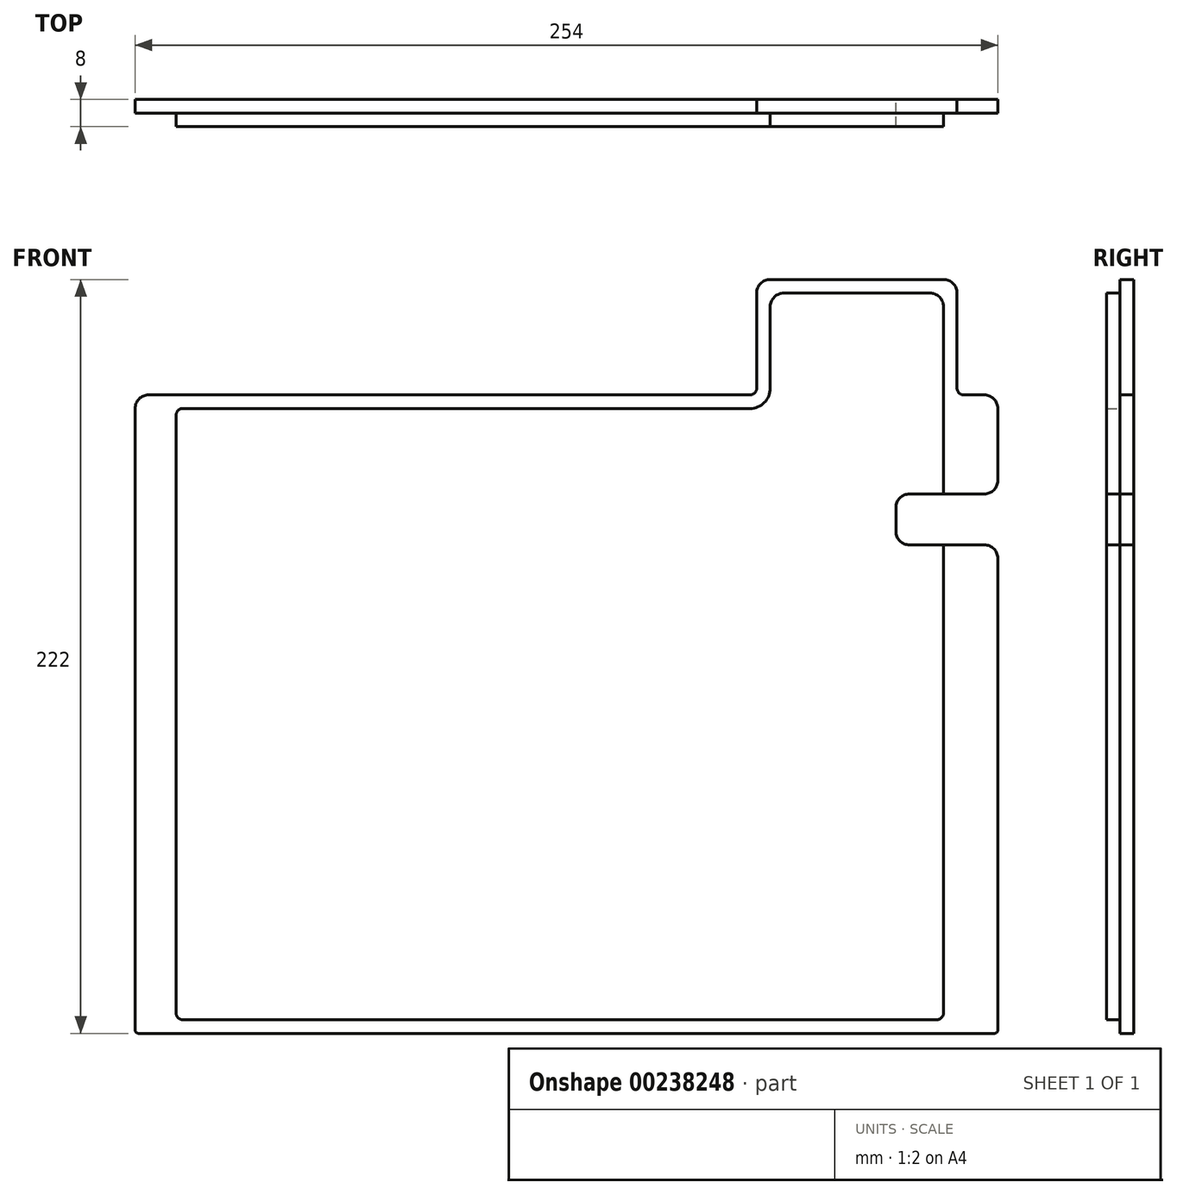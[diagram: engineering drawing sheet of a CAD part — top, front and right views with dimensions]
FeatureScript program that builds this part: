
annotation { "Feature Type Name" : "Feature", "Feature Type Description" : "" }
export const myFeature = defineFeature(function(context is Context, id is Id, definition is map)
    precondition{}
    {
        {
            var Q0;
            Q0=qCreatedBy(makeId("Front.planeOp"),FACE);
            var sketch = newSketch(context, id + "F0", { "sketchPlane" : qUnion([Q0])});
            skLineSegment(sketch, "E0.bottom", {"start": v(123, 94) * mm, "end": v(117, 94) * mm});
            skLineSegment(sketch, "E0.top", {"start": v(126, -94) * mm, "end": v(-126, -94) * mm});
            skLineSegment(sketch, "E0.left", {"start": v(127, 90) * mm, "end": v(127, 68.84) * mm});
            skLineSegment(sketch, "E0.right", {"start": v(-127, 90) * mm, "end": v(-127, -93) * mm});
            skPoint(sketch, "E0.middle", {"position": v(0, 0) * mm});
            skLineSegment(sketch, "E1.top", {"start": v(111, 128) * mm, "end": v(60, 128) * mm});
            skLineSegment(sketch, "E1.left", {"start": v(115, 96) * mm, "end": v(115, 124) * mm});
            skLineSegment(sketch, "E1.right", {"start": v(56, 96) * mm, "end": v(56, 124) * mm});
            skLineSegment(sketch, "E2.trimOffspring", {"start": v(54, 94) * mm, "end": v(-123, 94) * mm});
            skPoint(sketch, "E3.visualSharp", {"position": v(56, 128) * mm});
            skArc(sketch, "E3.filletArc", {"start": v(60, 128) * mm, "mid": v(57.17, 126.83) * mm, "end": v(56, 124) * mm});
            skPoint(sketch, "E4.visualSharp", {"position": v(115, 128) * mm});
            skArc(sketch, "E4.filletArc", {"start": v(115, 124) * mm, "mid": v(113.83, 126.83) * mm, "end": v(111, 128) * mm});
            skPoint(sketch, "E5.visualSharp", {"position": v(127, 94) * mm});
            skArc(sketch, "E5.filletArc", {"start": v(127, 90) * mm, "mid": v(125.83, 92.83) * mm, "end": v(123, 94) * mm});
            skPoint(sketch, "E6.visualSharp", {"position": v(-127, 94) * mm});
            skArc(sketch, "E6.filletArc", {"start": v(-123, 94) * mm, "mid": v(-125.83, 92.83) * mm, "end": v(-127, 90) * mm});
            skPoint(sketch, "E7.visualSharp", {"position": v(56, 94) * mm});
            skArc(sketch, "E7.filletArc", {"start": v(54, 94) * mm, "mid": v(55.41, 94.59) * mm, "end": v(56, 96) * mm});
            skPoint(sketch, "E8.visualSharp", {"position": v(115, 94) * mm});
            skArc(sketch, "E8.filletArc", {"start": v(115, 96) * mm, "mid": v(115.59, 94.59) * mm, "end": v(117, 94) * mm});
            skPoint(sketch, "E9.visualSharp", {"position": v(-127, -94) * mm});
            skArc(sketch, "E9.filletArc", {"start": v(-127, -93) * mm, "mid": v(-126.7, -93.7) * mm, "end": v(-126, -94) * mm});
            skPoint(sketch, "E10.visualSharp", {"position": v(127, -94) * mm});
            skArc(sketch, "E10.filletArc", {"start": v(126, -94) * mm, "mid": v(126.7, -93.7) * mm, "end": v(127, -93) * mm});
            skLineSegment(sketch, "E11.bottom", {"start": v(123, 64.84) * mm, "end": v(101, 64.84) * mm});
            skLineSegment(sketch, "E11.top", {"start": v(123, 49.84) * mm, "end": v(101, 49.84) * mm});
            skLineSegment(sketch, "E11.right", {"start": v(97, 60.84) * mm, "end": v(97, 53.84) * mm});
            skLineSegment(sketch, "E12.trimOffspring", {"start": v(127, 45.84) * mm, "end": v(127, -93) * mm});
            skPoint(sketch, "E13.visualSharp", {"position": v(97, 64.84) * mm});
            skArc(sketch, "E13.filletArc", {"start": v(101, 64.84) * mm, "mid": v(98.17, 63.67) * mm, "end": v(97, 60.84) * mm});
            skPoint(sketch, "E14.visualSharp", {"position": v(97, 49.84) * mm});
            skArc(sketch, "E14.filletArc", {"start": v(97, 53.84) * mm, "mid": v(98.17, 51.01) * mm, "end": v(101, 49.84) * mm});
            skPoint(sketch, "E15.visualSharp", {"position": v(127, 64.84) * mm});
            skArc(sketch, "E15.filletArc", {"start": v(123, 64.84) * mm, "mid": v(125.83, 66.01) * mm, "end": v(127, 68.84) * mm});
            skPoint(sketch, "E16.visualSharp", {"position": v(127, 49.84) * mm});
            skArc(sketch, "E16.filletArc", {"start": v(127, 45.84) * mm, "mid": v(125.83, 48.67) * mm, "end": v(123, 49.84) * mm});
            skSolve(sketch);
        }
        {
            var Q0;
            Q0=makeQuery(id+"F0.imprint","IMPRINT",FACE,{"disambiguationData":[TD([[makeQuery(id+"F0.imprint","IMPRINT",EDGE,{"derivedFrom":sQuery(id+"F0.wireOp",EDGE,"E0.bottom")}),1.0]])]});
            extrude(context, id + "F1", {"entities" : qUnion([Q0]), "depth" : 4 * mm});
        }
        {
            var Q0;
            Q0=makeQuery(id+"F1.opExtrude","CAP_FACE",FACE,{"disambiguationData":[OSD([sQuery(id+"F0.wireOp",EDGE,"E0.bottom"),sQuery(id+"F0.wireOp",EDGE,"E0.top"),sQuery(id+"F0.wireOp",EDGE,"E0.left"),sQuery(id+"F0.wireOp",EDGE,"E0.right"),sQuery(id+"F0.wireOp",EDGE,"E1.top"),sQuery(id+"F0.wireOp",EDGE,"E1.left"),sQuery(id+"F0.wireOp",EDGE,"E1.right"),sQuery(id+"F0.wireOp",EDGE,"E2.trimOffspring"),sQuery(id+"F0.wireOp",EDGE,"E3.filletArc"),sQuery(id+"F0.wireOp",EDGE,"E4.filletArc"),sQuery(id+"F0.wireOp",EDGE,"E5.filletArc"),sQuery(id+"F0.wireOp",EDGE,"E6.filletArc"),sQuery(id+"F0.wireOp",EDGE,"E7.filletArc"),sQuery(id+"F0.wireOp",EDGE,"E8.filletArc"),sQuery(id+"F0.wireOp",EDGE,"E9.filletArc"),sQuery(id+"F0.wireOp",EDGE,"E10.filletArc")])],"isStart":false});
            var sketch = newSketch(context, id + "F2", { "sketchPlane" : qUnion([Q0])});
            skLineSegment(sketch, "E17.0", {"start": v(123, 94) * mm, "end": v(117, 94) * mm, "construction": true});
            skLineSegment(sketch, "E17.1", {"start": v(126, -94) * mm, "end": v(-126, -94) * mm, "construction": true});
            skLineSegment(sketch, "E17.2", {"start": v(127, 90) * mm, "end": v(127, 68.84) * mm, "construction": true});
            skLineSegment(sketch, "E17.3", {"start": v(-127, 90) * mm, "end": v(-127, -93) * mm, "construction": true});
            skPoint(sketch, "E17.4", {"position": v(0, 0) * mm});
            skLineSegment(sketch, "E17.5", {"start": v(111, 128) * mm, "end": v(60, 128) * mm, "construction": true});
            skLineSegment(sketch, "E17.6", {"start": v(115, 96) * mm, "end": v(115, 124) * mm, "construction": true});
            skLineSegment(sketch, "E17.7", {"start": v(56, 96) * mm, "end": v(56, 124) * mm, "construction": true});
            skLineSegment(sketch, "E17.8", {"start": v(54, 94) * mm, "end": v(-123, 94) * mm, "construction": true});
            skPoint(sketch, "E17.9", {"position": v(56, 128) * mm});
            skArc(sketch, "E17.10", {"start": v(60, 128) * mm, "mid": v(57.17, 126.83) * mm, "end": v(56, 124) * mm, "construction": true});
            skPoint(sketch, "E17.11", {"position": v(115, 128) * mm});
            skArc(sketch, "E17.12", {"start": v(115, 124) * mm, "mid": v(113.83, 126.83) * mm, "end": v(111, 128) * mm, "construction": true});
            skPoint(sketch, "E17.13", {"position": v(127, 94) * mm});
            skArc(sketch, "E17.14", {"start": v(127, 90) * mm, "mid": v(125.83, 92.83) * mm, "end": v(123, 94) * mm, "construction": true});
            skPoint(sketch, "E17.15", {"position": v(-127, 94) * mm});
            skArc(sketch, "E17.16", {"start": v(-123, 94) * mm, "mid": v(-125.83, 92.83) * mm, "end": v(-127, 90) * mm, "construction": true});
            skPoint(sketch, "E17.17", {"position": v(56, 94) * mm});
            skArc(sketch, "E17.18", {"start": v(54, 94) * mm, "mid": v(55.41, 94.59) * mm, "end": v(56, 96) * mm, "construction": true});
            skPoint(sketch, "E17.19", {"position": v(115, 94) * mm});
            skArc(sketch, "E17.20", {"start": v(115, 96) * mm, "mid": v(115.59, 94.59) * mm, "end": v(117, 94) * mm, "construction": true});
            skPoint(sketch, "E17.21", {"position": v(-127, -94) * mm});
            skArc(sketch, "E17.22", {"start": v(-127, -93) * mm, "mid": v(-126.7, -93.7) * mm, "end": v(-126, -94) * mm, "construction": true});
            skPoint(sketch, "E17.23", {"position": v(127, -94) * mm});
            skArc(sketch, "E17.24", {"start": v(126, -94) * mm, "mid": v(126.7, -93.7) * mm, "end": v(127, -93) * mm, "construction": true});
            skArc(sketch, "E18.0", {"start": v(54, 90) * mm, "mid": v(58.24, 91.76) * mm, "end": v(60, 96) * mm});
            skLineSegment(sketch, "E18.1", {"start": v(54, 90) * mm, "end": v(-112.94, 90) * mm});
            skLineSegment(sketch, "E18.2", {"start": v(60, 96) * mm, "end": v(60, 120) * mm});
            skLineSegment(sketch, "E18.4", {"start": v(109, -90) * mm, "end": v(-112.94, -90) * mm});
            skLineSegment(sketch, "E18.6", {"start": v(107, 124) * mm, "end": v(64, 124) * mm});
            skLineSegment(sketch, "E18.7", {"start": v(111, 96) * mm, "end": v(111, 120) * mm});
            skLineSegment(sketch, "E19", {"start": v(-114.94, 88) * mm, "end": v(-114.94, -88) * mm});
            skLineSegment(sketch, "E20", {"start": v(111, 96) * mm, "end": v(111, 64.84) * mm});
            skPoint(sketch, "E21.visualSharp", {"position": v(-114.94, 90) * mm});
            skArc(sketch, "E21.filletArc", {"start": v(-112.94, 90) * mm, "mid": v(-114.35, 89.41) * mm, "end": v(-114.94, 88) * mm});
            skPoint(sketch, "E22.visualSharp", {"position": v(-114.94, -90) * mm});
            skArc(sketch, "E22.filletArc", {"start": v(-114.94, -88) * mm, "mid": v(-114.35, -89.41) * mm, "end": v(-112.94, -90) * mm});
            skPoint(sketch, "E23.visualSharp", {"position": v(111, -90) * mm});
            skArc(sketch, "E23.filletArc", {"start": v(109, -90) * mm, "mid": v(110.41, -89.41) * mm, "end": v(111, -88) * mm});
            skArc(sketch, "E24.filletArc", {"start": v(64, 124) * mm, "mid": v(61.17, 122.83) * mm, "end": v(60, 120) * mm});
            skArc(sketch, "E25.filletArc", {"start": v(111, 120) * mm, "mid": v(109.83, 122.83) * mm, "end": v(107, 124) * mm});
            skLineSegment(sketch, "E26.0", {"start": v(111, 64.84) * mm, "end": v(101, 64.84) * mm});
            skArc(sketch, "E26.1", {"start": v(101, 64.84) * mm, "mid": v(98.17, 63.67) * mm, "end": v(97, 60.84) * mm});
            skLineSegment(sketch, "E26.2", {"start": v(97, 60.84) * mm, "end": v(97, 53.84) * mm});
            skArc(sketch, "E26.3", {"start": v(97, 53.84) * mm, "mid": v(98.17, 51.01) * mm, "end": v(101, 49.84) * mm});
            skLineSegment(sketch, "E26.4", {"start": v(111, 49.84) * mm, "end": v(101, 49.84) * mm});
            skPoint(sketch, "E27.orphan", {"position": v(123, 64.84) * mm});
            skPoint(sketch, "E28.orphan", {"position": v(123, 49.84) * mm});
            skLineSegment(sketch, "E29.trimOffspring", {"start": v(111, 49.84) * mm, "end": v(111, -88) * mm});
            skSolve(sketch);
        }
        {
            var Q0;
            Q0=qSketchRegion(id+"F2",true);
            extrude(context, id + "F3", {"entities" : qUnion([Q0]), "depth" : 4 * mm});
        }
    });
